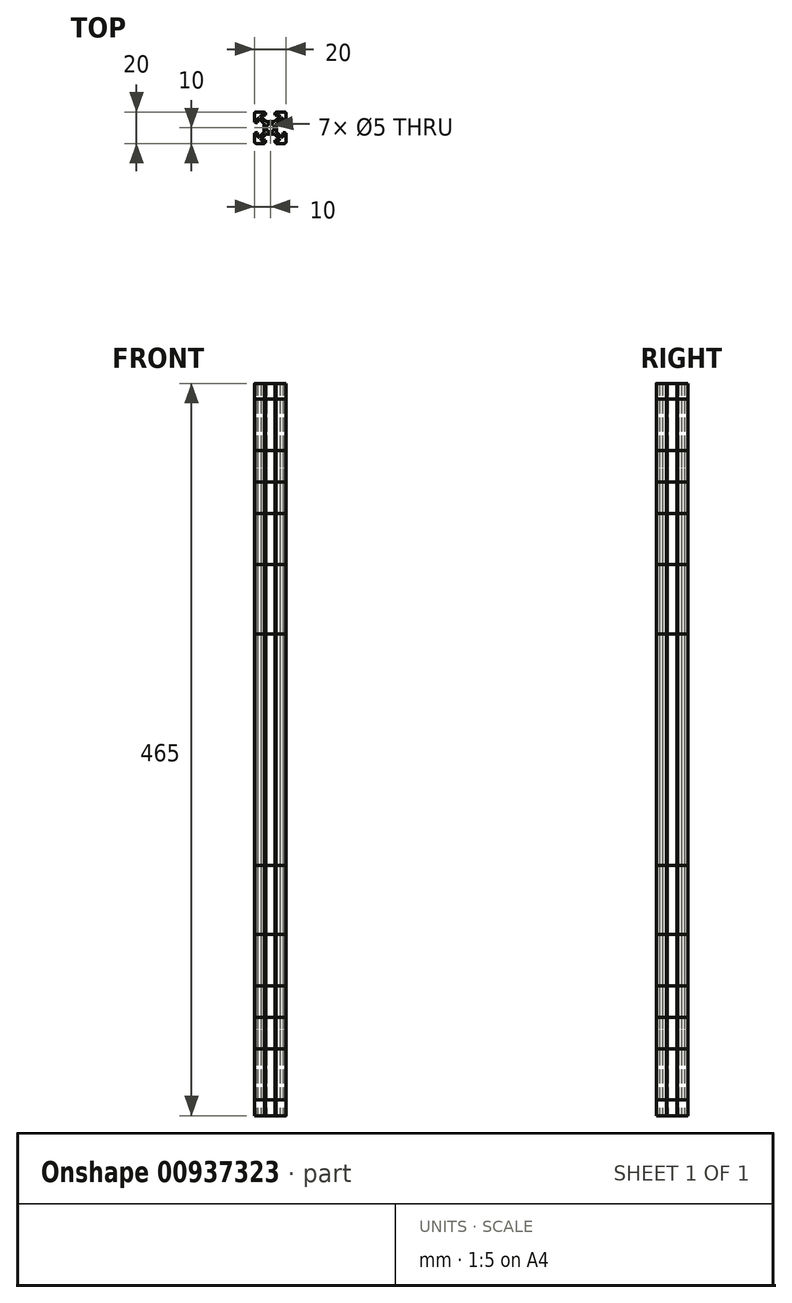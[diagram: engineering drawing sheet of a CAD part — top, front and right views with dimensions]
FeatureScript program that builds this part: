
annotation { "Feature Type Name" : "Feature", "Feature Type Description" : "" }
export const myFeature = defineFeature(function(context is Context, id is Id, definition is map)
    precondition{}
    {
        {
            var Q0;
            Q0=qCreatedBy(makeId("Top.planeOp"),FACE);
            var sketch = newSketch(context, id + "F0", { "sketchPlane" : qUnion([Q0])});
            skLineSegment(sketch, "E0", {"start": v(0, 0) * mm, "end": v(-7.98, 7.98) * mm, "construction": true});
            skLineSegment(sketch, "E1", {"start": v(-5.87, 7.15) * mm, "end": v(-3.02, 4.3) * mm});
            skLineSegment(sketch, "E2", {"start": v(-7.15, 5.87) * mm, "end": v(-4.3, 3.02) * mm});
            skLineSegment(sketch, "E3", {"start": v(0, 4) * mm, "end": v(-2.31, 4) * mm});
            skLineSegment(sketch, "E4", {"start": v(-4, 0) * mm, "end": v(-4, 2.31) * mm});
            skLineSegment(sketch, "E5", {"start": v(-3.6, 10) * mm, "end": v(-9, 10) * mm});
            skLineSegment(sketch, "E6", {"start": v(-10, 9) * mm, "end": v(-10, 3.6) * mm});
            skLineSegment(sketch, "E7", {"start": v(-3.1, 8) * mm, "end": v(-5.52, 8) * mm});
            skLineSegment(sketch, "E8", {"start": v(-8, 3.1) * mm, "end": v(-8, 5.52) * mm});
            skLineSegment(sketch, "E9", {"start": v(-8, 3.1) * mm, "end": v(-9.5, 3.1) * mm});
            skLineSegment(sketch, "E10", {"start": v(-3.1, 9.5) * mm, "end": v(-3.1, 8) * mm});
            skLineSegment(sketch, "E11", {"start": v(-3.6, 10) * mm, "end": v(-3.6, 9.5) * mm});
            skLineSegment(sketch, "E12", {"start": v(-3.6, 9.5) * mm, "end": v(-3.1, 9.5) * mm});
            skLineSegment(sketch, "E13", {"start": v(-10, 3.6) * mm, "end": v(-9.5, 3.6) * mm});
            skLineSegment(sketch, "E14", {"start": v(-9.5, 3.6) * mm, "end": v(-9.5, 3.1) * mm});
            skPoint(sketch, "E15.visualSharp", {"position": v(-10, 10) * mm});
            skArc(sketch, "E15.filletArc", {"start": v(-9, 10) * mm, "mid": v(-9.7, 9.7) * mm, "end": v(-10, 9) * mm});
            skPoint(sketch, "E16.visualSharp", {"position": v(-2.73, 4) * mm});
            skArc(sketch, "E16.filletArc", {"start": v(-3.02, 4.3) * mm, "mid": v(-2.7, 4.08) * mm, "end": v(-2.31, 4) * mm});
            skPoint(sketch, "E17.visualSharp", {"position": v(-4, 2.73) * mm});
            skArc(sketch, "E17.filletArc", {"start": v(-4, 2.31) * mm, "mid": v(-4.08, 2.7) * mm, "end": v(-4.3, 3.02) * mm});
            skPoint(sketch, "E18.visualSharp", {"position": v(-8, 6.73) * mm});
            skArc(sketch, "E18.filletArc", {"start": v(-7.15, 5.87) * mm, "mid": v(-7.7, 5.98) * mm, "end": v(-8, 5.52) * mm});
            skPoint(sketch, "E19.visualSharp", {"position": v(-6.73, 8) * mm});
            skArc(sketch, "E19.filletArc", {"start": v(-5.52, 8) * mm, "mid": v(-5.98, 7.7) * mm, "end": v(-5.87, 7.15) * mm});
            skLineSegment(sketch, "E20", {"start": v(0, 8.4) * mm, "end": v(0, -5.34) * mm, "construction": true});
            skArc(sketch, "E21.MirrorCS", {"start": v(-4.3, 3.02) * mm, "mid": v(-4.08, 2.7) * mm, "end": v(-4, 2.31) * mm});
            skArc(sketch, "E22.MirrorCS", {"start": v(-2.31, 4) * mm, "mid": v(-2.7, 4.08) * mm, "end": v(-3.02, 4.3) * mm});
            skArc(sketch, "E23.MirrorCS", {"start": v(-5.87, 7.15) * mm, "mid": v(-5.98, 7.7) * mm, "end": v(-5.52, 8) * mm});
            skArc(sketch, "E24.MirrorCS", {"start": v(-10, 9) * mm, "mid": v(-9.7, 9.7) * mm, "end": v(-9, 10) * mm});
            skLineSegment(sketch, "E25.MirrorCS", {"start": v(-3.1, 8) * mm, "end": v(-3.1, 9.5) * mm});
            skLineSegment(sketch, "E26.MirrorCS", {"start": v(-10, 3.6) * mm, "end": v(-10, 9) * mm});
            skLineSegment(sketch, "E27.MirrorCS", {"start": v(-9, 10) * mm, "end": v(-3.6, 10) * mm});
            skLineSegment(sketch, "E28.MirrorCS", {"start": v(-9.5, 3.1) * mm, "end": v(-8, 3.1) * mm});
            skArc(sketch, "E29.MirrorCS", {"start": v(-8, 5.52) * mm, "mid": v(-7.7, 5.98) * mm, "end": v(-7.15, 5.87) * mm});
            skLineSegment(sketch, "E30.MirrorCS", {"start": v(-8.4, 0) * mm, "end": v(5.34, 0) * mm, "construction": true});
            skArc(sketch, "E31.MirrorCS", {"start": v(2.31, 4) * mm, "mid": v(2.7, 4.08) * mm, "end": v(3.02, 4.3) * mm});
            skLineSegment(sketch, "E32.MirrorCS", {"start": v(3.6, 10) * mm, "end": v(3.6, 9.5) * mm});
            skLineSegment(sketch, "E33.MirrorCS", {"start": v(9.5, 3.6) * mm, "end": v(9.5, 3.1) * mm});
            skLineSegment(sketch, "E34.MirrorCS", {"start": v(10, 3.6) * mm, "end": v(9.5, 3.6) * mm});
            skLineSegment(sketch, "E35.MirrorCS", {"start": v(3.6, 9.5) * mm, "end": v(3.1, 9.5) * mm});
            skArc(sketch, "E36.MirrorCS", {"start": v(4.3, 3.02) * mm, "mid": v(4.08, 2.7) * mm, "end": v(4, 2.31) * mm});
            skArc(sketch, "E37.MirrorCS", {"start": v(3.02, 4.3) * mm, "mid": v(2.7, 4.08) * mm, "end": v(2.31, 4) * mm});
            skArc(sketch, "E38.MirrorCS", {"start": v(4, 2.31) * mm, "mid": v(4.08, 2.7) * mm, "end": v(4.3, 3.02) * mm});
            skArc(sketch, "E39.MirrorCS", {"start": v(10, 9) * mm, "mid": v(9.7, 9.7) * mm, "end": v(9, 10) * mm});
            skArc(sketch, "E40.MirrorCS", {"start": v(8, 5.52) * mm, "mid": v(7.7, 5.98) * mm, "end": v(7.15, 5.87) * mm});
            skArc(sketch, "E41.MirrorCS", {"start": v(9, 10) * mm, "mid": v(9.7, 9.7) * mm, "end": v(10, 9) * mm});
            skLineSegment(sketch, "E42.MirrorCS", {"start": v(8, 3.1) * mm, "end": v(8, 5.52) * mm});
            skLineSegment(sketch, "E43.MirrorCS", {"start": v(3.1, 8) * mm, "end": v(5.52, 8) * mm});
            skPoint(sketch, "E44.MirrorP", {"position": v(2.73, 4) * mm});
            skPoint(sketch, "E45.MirrorP", {"position": v(4, 2.73) * mm});
            skLineSegment(sketch, "E46.MirrorCS", {"start": v(0, 4) * mm, "end": v(2.31, 4) * mm});
            skPoint(sketch, "E47.MirrorP", {"position": v(8, 6.73) * mm});
            skPoint(sketch, "E48.MirrorP", {"position": v(10, 10) * mm});
            skLineSegment(sketch, "E49.MirrorCS", {"start": v(7.15, 5.87) * mm, "end": v(4.3, 3.02) * mm});
            skArc(sketch, "E50.MirrorCS", {"start": v(7.15, 5.87) * mm, "mid": v(7.7, 5.98) * mm, "end": v(8, 5.52) * mm});
            skLineSegment(sketch, "E51.MirrorCS", {"start": v(3.6, 10) * mm, "end": v(9, 10) * mm});
            skLineSegment(sketch, "E52.MirrorCS", {"start": v(10, 9) * mm, "end": v(10, 3.6) * mm});
            skLineSegment(sketch, "E53.MirrorCS", {"start": v(3.1, 9.5) * mm, "end": v(3.1, 8) * mm});
            skArc(sketch, "E54.MirrorCS", {"start": v(5.87, 7.15) * mm, "mid": v(5.98, 7.7) * mm, "end": v(5.52, 8) * mm});
            skLineSegment(sketch, "E55.MirrorCS", {"start": v(4, 0) * mm, "end": v(4, 2.31) * mm});
            skPoint(sketch, "E56.MirrorP", {"position": v(6.73, 8) * mm});
            skLineSegment(sketch, "E57.MirrorCS", {"start": v(5.87, 7.15) * mm, "end": v(3.02, 4.3) * mm});
            skLineSegment(sketch, "E58.MirrorCS", {"start": v(9.5, 3.1) * mm, "end": v(8, 3.1) * mm});
            skArc(sketch, "E59.MirrorCS", {"start": v(5.52, 8) * mm, "mid": v(5.98, 7.7) * mm, "end": v(5.87, 7.15) * mm});
            skLineSegment(sketch, "E60.MirrorCS", {"start": v(8, 3.1) * mm, "end": v(9.5, 3.1) * mm});
            skLineSegment(sketch, "E61.MirrorCS", {"start": v(3.1, 8) * mm, "end": v(3.1, 9.5) * mm});
            skLineSegment(sketch, "E62.MirrorCS", {"start": v(9, 10) * mm, "end": v(3.6, 10) * mm});
            skLineSegment(sketch, "E63.MirrorCS", {"start": v(10, 3.6) * mm, "end": v(10, 9) * mm});
            skArc(sketch, "E64.MirrorCS", {"start": v(-3.02, -4.3) * mm, "mid": v(-2.7, -4.08) * mm, "end": v(-2.31, -4) * mm});
            skArc(sketch, "E65.MirrorCS", {"start": v(4, -2.31) * mm, "mid": v(4.08, -2.7) * mm, "end": v(4.3, -3.02) * mm});
            skLineSegment(sketch, "E66.MirrorCS", {"start": v(3.6, -9.5) * mm, "end": v(3.1, -9.5) * mm});
            skLineSegment(sketch, "E67.MirrorCS", {"start": v(-9.5, -3.6) * mm, "end": v(-9.5, -3.1) * mm});
            skLineSegment(sketch, "E68.MirrorCS", {"start": v(3.6, -10) * mm, "end": v(3.6, -9.5) * mm});
            skLineSegment(sketch, "E69.MirrorCS", {"start": v(-10, -3.6) * mm, "end": v(-9.5, -3.6) * mm});
            skArc(sketch, "E70.MirrorCS", {"start": v(-4.3, -3.02) * mm, "mid": v(-4.08, -2.7) * mm, "end": v(-4, -2.31) * mm});
            skLineSegment(sketch, "E71.MirrorCS", {"start": v(-3.6, -10) * mm, "end": v(-3.6, -9.5) * mm});
            skLineSegment(sketch, "E72.MirrorCS", {"start": v(-3.6, -9.5) * mm, "end": v(-3.1, -9.5) * mm});
            skArc(sketch, "E73.MirrorCS", {"start": v(2.31, -4) * mm, "mid": v(2.7, -4.08) * mm, "end": v(3.02, -4.3) * mm});
            skLineSegment(sketch, "E74.MirrorCS", {"start": v(9.5, -3.6) * mm, "end": v(9.5, -3.1) * mm});
            skLineSegment(sketch, "E75.MirrorCS", {"start": v(10, -3.6) * mm, "end": v(9.5, -3.6) * mm});
            skArc(sketch, "E76.MirrorCS", {"start": v(-4, -2.31) * mm, "mid": v(-4.08, -2.7) * mm, "end": v(-4.3, -3.02) * mm});
            skArc(sketch, "E77.MirrorCS", {"start": v(-2.31, -4) * mm, "mid": v(-2.7, -4.08) * mm, "end": v(-3.02, -4.3) * mm});
            skArc(sketch, "E78.MirrorCS", {"start": v(4.3, -3.02) * mm, "mid": v(4.08, -2.7) * mm, "end": v(4, -2.31) * mm});
            skArc(sketch, "E79.MirrorCS", {"start": v(3.02, -4.3) * mm, "mid": v(2.7, -4.08) * mm, "end": v(2.31, -4) * mm});
            skArc(sketch, "E80.MirrorCS", {"start": v(-5.87, -7.15) * mm, "mid": v(-5.98, -7.7) * mm, "end": v(-5.52, -8) * mm});
            skPoint(sketch, "E81.MirrorP", {"position": v(2.73, -4) * mm});
            skLineSegment(sketch, "E82.MirrorCS", {"start": v(-8, -3.1) * mm, "end": v(-8, -5.52) * mm});
            skPoint(sketch, "E83.MirrorP", {"position": v(-6.73, -8) * mm});
            skLineSegment(sketch, "E84.MirrorCS", {"start": v(-5.87, -7.15) * mm, "end": v(-3.02, -4.3) * mm});
            skLineSegment(sketch, "E85.MirrorCS", {"start": v(-4, 0) * mm, "end": v(-4, -2.31) * mm});
            skLineSegment(sketch, "E86.MirrorCS", {"start": v(10, -3.6) * mm, "end": v(10, -9) * mm});
            skLineSegment(sketch, "E87.MirrorCS", {"start": v(-7.15, -5.87) * mm, "end": v(-4.3, -3.02) * mm});
            skArc(sketch, "E88.MirrorCS", {"start": v(5.52, -8) * mm, "mid": v(5.98, -7.7) * mm, "end": v(5.87, -7.15) * mm});
            skLineSegment(sketch, "E89.MirrorCS", {"start": v(0, -4) * mm, "end": v(-2.31, -4) * mm});
            skArc(sketch, "E90.MirrorCS", {"start": v(-9, -10) * mm, "mid": v(-9.7, -9.7) * mm, "end": v(-10, -9) * mm});
            skPoint(sketch, "E91.MirrorP", {"position": v(8, -6.73) * mm});
            skPoint(sketch, "E92.MirrorP", {"position": v(6.73, -8) * mm});
            skLineSegment(sketch, "E93.MirrorCS", {"start": v(0, -4) * mm, "end": v(2.31, -4) * mm});
            skPoint(sketch, "E94.MirrorP", {"position": v(10, -10) * mm});
            skPoint(sketch, "E95.MirrorP", {"position": v(-8, -6.73) * mm});
            skLineSegment(sketch, "E96.MirrorCS", {"start": v(8, -3.1) * mm, "end": v(8, -5.52) * mm});
            skLineSegment(sketch, "E97.MirrorCS", {"start": v(-9.5, -3.1) * mm, "end": v(-8, -3.1) * mm});
            skArc(sketch, "E98.MirrorCS", {"start": v(9, -10) * mm, "mid": v(9.7, -9.7) * mm, "end": v(10, -9) * mm});
            skLineSegment(sketch, "E99.MirrorCS", {"start": v(-3.1, -8) * mm, "end": v(-5.52, -8) * mm});
            skArc(sketch, "E100.MirrorCS", {"start": v(7.15, -5.87) * mm, "mid": v(7.7, -5.98) * mm, "end": v(8, -5.52) * mm});
            skArc(sketch, "E101.MirrorCS", {"start": v(-7.15, -5.87) * mm, "mid": v(-7.7, -5.98) * mm, "end": v(-8, -5.52) * mm});
            skLineSegment(sketch, "E102.MirrorCS", {"start": v(3.1, -8) * mm, "end": v(3.1, -9.5) * mm});
            skPoint(sketch, "E103.MirrorP", {"position": v(4, -2.73) * mm});
            skPoint(sketch, "E104.MirrorP", {"position": v(-10, -10) * mm});
            skLineSegment(sketch, "E105.MirrorCS", {"start": v(4, 0) * mm, "end": v(4, -2.31) * mm});
            skPoint(sketch, "E106.MirrorP", {"position": v(-4, -2.73) * mm});
            skLineSegment(sketch, "E107.MirrorCS", {"start": v(-3.6, -10) * mm, "end": v(-9, -10) * mm});
            skLineSegment(sketch, "E108.MirrorCS", {"start": v(7.15, -5.87) * mm, "end": v(4.3, -3.02) * mm});
            skLineSegment(sketch, "E109.MirrorCS", {"start": v(8, -3.1) * mm, "end": v(9.5, -3.1) * mm});
            skLineSegment(sketch, "E110.MirrorCS", {"start": v(3.1, -8) * mm, "end": v(5.52, -8) * mm});
            skLineSegment(sketch, "E111.MirrorCS", {"start": v(5.87, -7.15) * mm, "end": v(3.02, -4.3) * mm});
            skPoint(sketch, "E112.MirrorP", {"position": v(-2.73, -4) * mm});
            skLineSegment(sketch, "E113.MirrorCS", {"start": v(-3.1, -8) * mm, "end": v(-3.1, -9.5) * mm});
            skLineSegment(sketch, "E114.MirrorCS", {"start": v(3.6, -10) * mm, "end": v(9, -10) * mm});
            skLineSegment(sketch, "E115.MirrorCS", {"start": v(-10, -9) * mm, "end": v(-10, -3.6) * mm});
            skLineSegment(sketch, "E116.MirrorCS", {"start": v(-8, -3.1) * mm, "end": v(-9.5, -3.1) * mm});
            skArc(sketch, "E117.MirrorCS", {"start": v(5.87, -7.15) * mm, "mid": v(5.98, -7.7) * mm, "end": v(5.52, -8) * mm});
            skLineSegment(sketch, "E118.MirrorCS", {"start": v(9, -10) * mm, "end": v(3.6, -10) * mm});
            skLineSegment(sketch, "E119.MirrorCS", {"start": v(-10, -3.6) * mm, "end": v(-10, -9) * mm});
            skLineSegment(sketch, "E120.MirrorCS", {"start": v(-9, -10) * mm, "end": v(-3.6, -10) * mm});
            skArc(sketch, "E121.MirrorCS", {"start": v(10, -9) * mm, "mid": v(9.7, -9.7) * mm, "end": v(9, -10) * mm});
            skArc(sketch, "E122.MirrorCS", {"start": v(-10, -9) * mm, "mid": v(-9.7, -9.7) * mm, "end": v(-9, -10) * mm});
            skLineSegment(sketch, "E123.MirrorCS", {"start": v(3.1, -9.5) * mm, "end": v(3.1, -8) * mm});
            skArc(sketch, "E124.MirrorCS", {"start": v(-8, -5.52) * mm, "mid": v(-7.7, -5.98) * mm, "end": v(-7.15, -5.87) * mm});
            skLineSegment(sketch, "E125.MirrorCS", {"start": v(10, -9) * mm, "end": v(10, -3.6) * mm});
            skLineSegment(sketch, "E126.MirrorCS", {"start": v(9.5, -3.1) * mm, "end": v(8, -3.1) * mm});
            skLineSegment(sketch, "E127.MirrorCS", {"start": v(-3.1, -9.5) * mm, "end": v(-3.1, -8) * mm});
            skArc(sketch, "E128.MirrorCS", {"start": v(8, -5.52) * mm, "mid": v(7.7, -5.98) * mm, "end": v(7.15, -5.87) * mm});
            skArc(sketch, "E129.MirrorCS", {"start": v(-5.52, -8) * mm, "mid": v(-5.98, -7.7) * mm, "end": v(-5.87, -7.15) * mm});
            skCircle(sketch, "E130", {"center": v(0, 0) * mm, "radius": 2.5 * mm});
            skSolve(sketch);
        }
        {
            var Q0;
            Q0 = qSketchRegion(id + "F0", true);
            extrude(context, id + "F1", {"entities" : qUnion([Q0]), "depth" : 445 * mm, "offsetDistance" : 25 * mm, "symmetric" : true});
        }
        {
            var Q0;
            Q0 = qSketchRegion(id + "F0", true);
            extrude(context, id + "F2", {"entities" : qUnion([Q0]), "depth" : 380 * mm, "offsetDistance" : 25 * mm, "symmetric" : true});
        }
        {
            var Q0;
            Q0 = qSketchRegion(id + "F0", true);
            extrude(context, id + "F3", {"entities" : qUnion([Q0]), "depth" : 465 * mm, "offsetDistance" : 25 * mm, "symmetric" : true});
        }
        {
            var Q0;
            Q0 = qSketchRegion(id + "F0", true);
            extrude(context, id + "F4", {"entities" : qUnion([Q0]), "depth" : 340 * mm, "offsetDistance" : 25 * mm, "symmetric" : true});
        }
        {
            var Q0;
            Q0 = qSketchRegion(id + "F0", true);
            extrude(context, id + "F5", {"entities" : qUnion([Q0]), "depth" : 300 * mm, "offsetDistance" : 25 * mm, "symmetric" : true});
        }
        {
            var Q0;
            Q0 = qSketchRegion(id + "F0", true);
            extrude(context, id + "F6", {"entities" : qUnion([Q0]), "depth" : 235 * mm, "offsetDistance" : 25 * mm, "symmetric" : true});
        }
        {
            var Q0;
            Q0 = qSketchRegion(id + "F0", true);
            extrude(context, id + "F7", {"entities" : qUnion([Q0]), "depth" : 147 * mm, "offsetDistance" : 25 * mm, "symmetric" : true});
        }
    });
